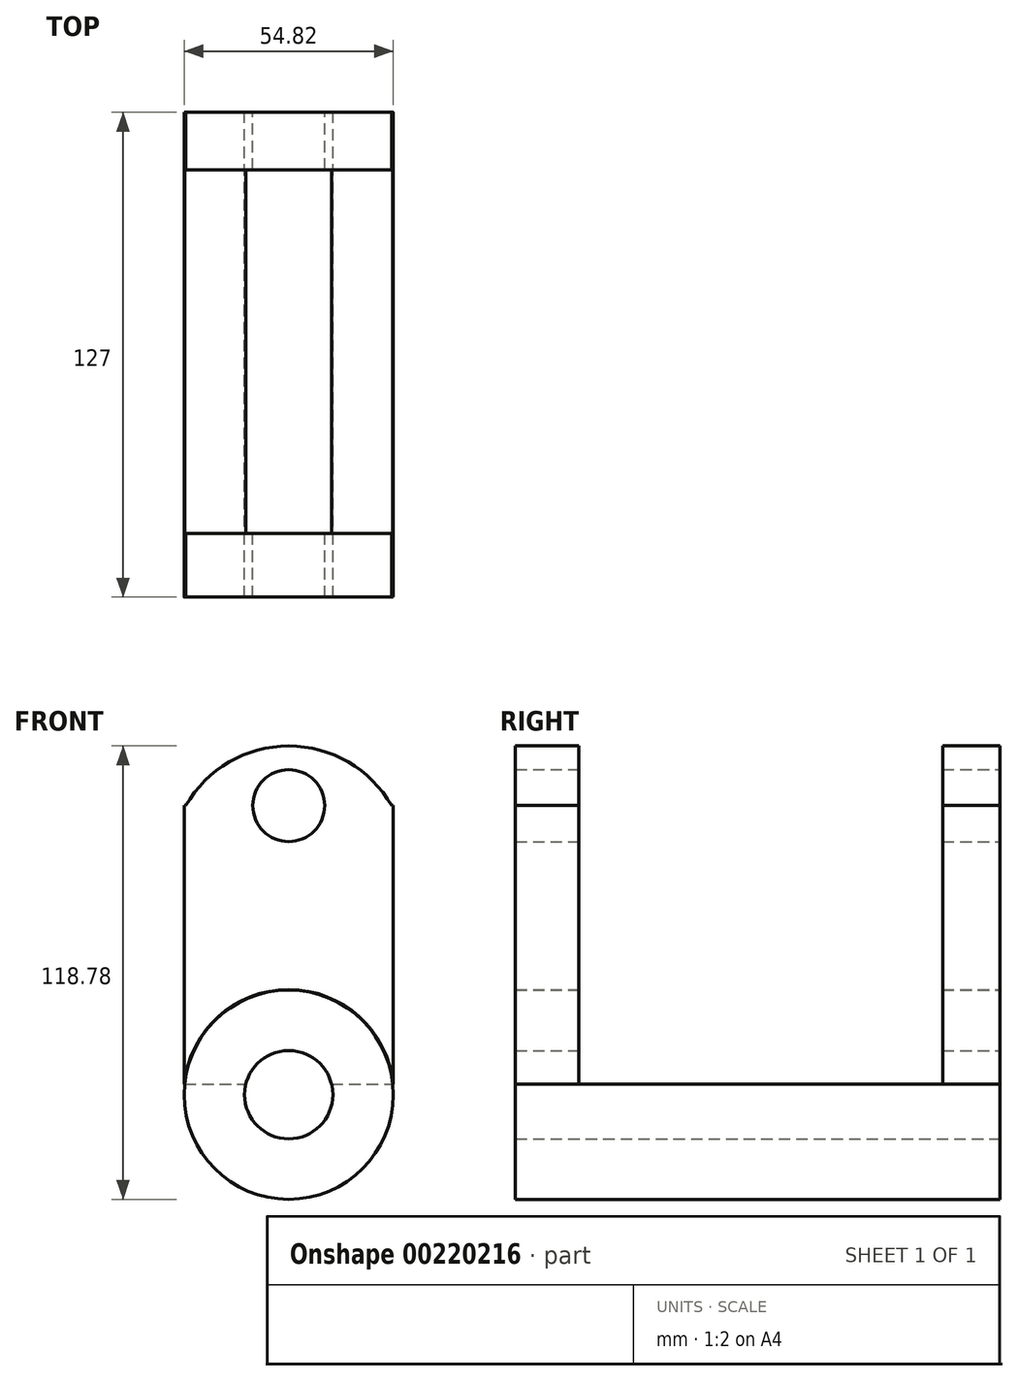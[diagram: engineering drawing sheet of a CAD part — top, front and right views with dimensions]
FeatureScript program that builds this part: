
annotation { "Feature Type Name" : "Feature", "Feature Type Description" : "" }
export const myFeature = defineFeature(function(context is Context, id is Id, definition is map)
    precondition{}
    {
        {
            var Q0;
            Q0=qCreatedBy(makeId("Front.planeOp"),FACE);
            var sketch = newSketch(context, id + "F0", { "sketchPlane" : qUnion([Q0])});
            skCircle(sketch, "E0", {"center": v(0, 0) * mm, "radius": 27.41 * mm});
            skCircle(sketch, "E1", {"center": v(0, 0) * mm, "radius": 11.57 * mm});
            skSolve(sketch);
        }
        {
            var Q0;
            Q0 = qSketchRegion(id + "F0", true);
            extrude(context, id + "F1", {"entities" : qUnion([Q0]), "depth" : 127 * mm});
        }
        {
            var Q0;
            Q0=qCreatedBy(makeId("Front.planeOp"),FACE);
            var sketch = newSketch(context, id + "F2", { "sketchPlane" : qUnion([Q0])});
            skLineSegment(sketch, "E2.bottom", {"start": v(-27.38, 75.73) * mm, "end": v(-26.95, 75.73) * mm});
            skLineSegment(sketch, "E2.left", {"start": v(-27.38, 75.73) * mm, "end": v(-27.38, -2.81) * mm});
            skLineSegment(sketch, "E2.right", {"start": v(27.38, 75.73) * mm, "end": v(27.38, -2.81) * mm});
            skPoint(sketch, "E2.middle", {"position": v(0, 0) * mm});
            skArc(sketch, "E3", {"start": v(27.38, 2.81) * mm, "mid": v(0, 27.53) * mm, "end": v(-27.38, 2.81) * mm});
            skPoint(sketch, "E2.top.end.orphan", {"position": v(27.38, -75.73) * mm});
            skPoint(sketch, "E2.top.start.orphan", {"position": v(-27.38, -75.73) * mm});
            skArc(sketch, "E4.trimOffspring", {"start": v(27.38, 74.94) * mm, "mid": v(0, 91.37) * mm, "end": v(-27.38, 74.94) * mm});
            skCircle(sketch, "E5", {"center": v(0, 75.73) * mm, "radius": 9.41 * mm});
            skLineSegment(sketch, "E6.trimOffspring", {"start": v(-9.41, 75.73) * mm, "end": v(9.41, 75.73) * mm});
            skLineSegment(sketch, "E7.trimOffspring", {"start": v(26.95, 75.73) * mm, "end": v(27.38, 75.73) * mm});
            skLineSegment(sketch, "E8", {"start": v(-9.41, 75.73) * mm, "end": v(-26.95, 75.73) * mm});
            skLineSegment(sketch, "E9", {"start": v(9.41, 75.73) * mm, "end": v(27.38, 75.73) * mm});
            skSolve(sketch);
        }
        {
            var Q0;
            Q0 = qSketchRegion(id + "F2", true);
            extrude(context, id + "F3", {"entities" : qUnion([Q0]), "depth" : 127 * mm});
        }
        {
            var Q0;
            Q0=makeQuery(id+"F3.opExtrude","SWEPT_FACE",FACE,{"disambiguationData":[OSD([sQuery(id+"F2.wireOp",EDGE,"E2.right")])]});
            var sketch = newSketch(context, id + "F4", { "sketchPlane" : qUnion([Q0])});
            skLineSegment(sketch, "E10.bottom", {"start": v(-110.38, 75.73) * mm, "end": v(-15.05, 75.73) * mm});
            skLineSegment(sketch, "E10.top", {"start": v(-110.38, 2.81) * mm, "end": v(-15.05, 2.81) * mm});
            skLineSegment(sketch, "E10.left", {"start": v(-110.38, 75.73) * mm, "end": v(-110.38, 2.81) * mm});
            skLineSegment(sketch, "E10.right", {"start": v(-15.05, 75.73) * mm, "end": v(-15.05, 2.81) * mm});
            skLineSegment(sketch, "E11.top", {"start": v(-110.38, 94.59) * mm, "end": v(-15.05, 94.59) * mm});
            skLineSegment(sketch, "E11.left", {"start": v(-110.38, 75.73) * mm, "end": v(-110.38, 94.59) * mm});
            skLineSegment(sketch, "E11.right", {"start": v(-15.05, 75.73) * mm, "end": v(-15.05, 94.59) * mm});
            skSolve(sketch);
        }
        {
            var Q0;
            Q0 = qSketchRegion(id + "F4", true);
            extrude(context, id + "F5", {"entities" : qUnion([Q0]), "operationType" : NewBodyOperationType.REMOVE, "endBound" : BoundingType.THROUGH_ALL, "oppositeDirection" : true, "depth" : 25.4 * mm});
        }
        {
            var Q0;
            Q0 = qSketchRegion(id + "F4", true);
            extrude(context, id + "F6", {"entities" : qUnion([Q0]), "operationType" : NewBodyOperationType.REMOVE, "endBound" : BoundingType.THROUGH_ALL, "oppositeDirection" : true, "depth" : 25.4 * mm});
        }
    });
